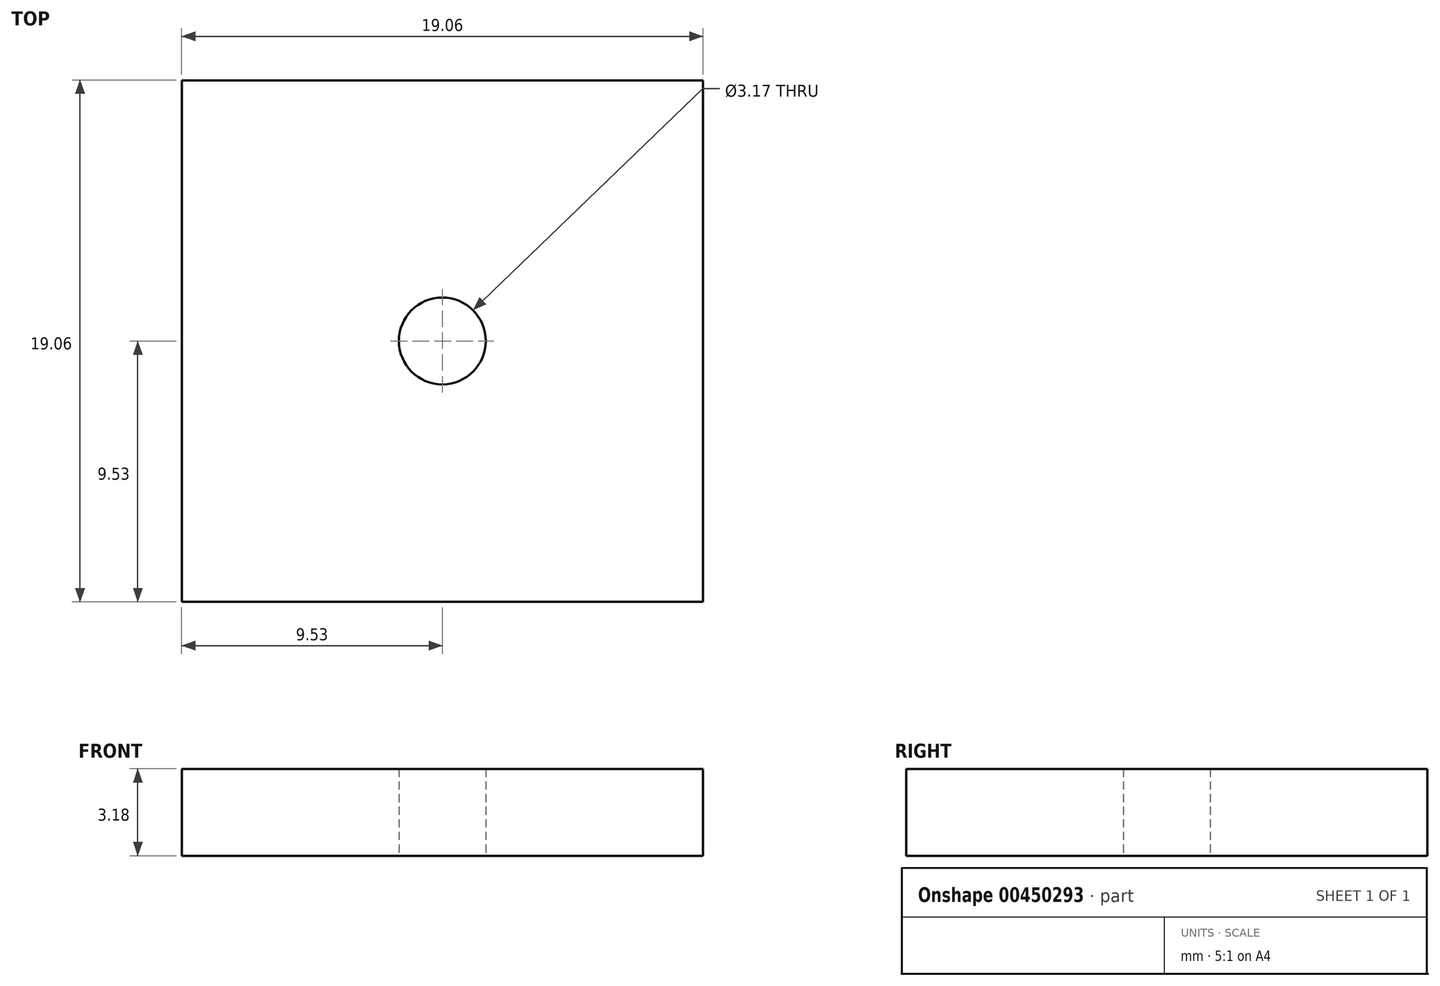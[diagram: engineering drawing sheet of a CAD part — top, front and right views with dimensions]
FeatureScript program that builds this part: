
annotation { "Feature Type Name" : "Feature", "Feature Type Description" : "" }
export const myFeature = defineFeature(function(context is Context, id is Id, definition is map)
    precondition{}
    {
        {
            var Q0;
            Q0=qCreatedBy(makeId("Top.planeOp"),FACE);
            var sketch = newSketch(context, id + "F0", { "sketchPlane" : qUnion([Q0])});
            skLineSegment(sketch, "E0.bottom", {"start": v(-9.52, -9.52) * mm, "end": v(9.53, -9.52) * mm});
            skLineSegment(sketch, "E0.top", {"start": v(-9.53, 9.52) * mm, "end": v(9.52, 9.52) * mm});
            skLineSegment(sketch, "E0.left", {"start": v(-9.52, -9.52) * mm, "end": v(-9.53, 9.52) * mm});
            skLineSegment(sketch, "E0.right", {"start": v(9.53, -9.52) * mm, "end": v(9.52, 9.52) * mm});
            skPoint(sketch, "E0.middle", {"position": v(0, 0) * mm});
            skCircle(sketch, "E1", {"center": v(0, 0) * mm, "radius": 1.59 * mm});
            skSolve(sketch);
        }
        {
            var Q0;
            Q0=makeQuery(id+"F0.imprint","IMPRINT",FACE,{"disambiguationData":[TD([[makeQuery(id+"F0.imprint","IMPRINT",EDGE,{"derivedFrom":sQuery(id+"F0.wireOp",EDGE,"E0.bottom")}),1.0]])]});
            extrude(context, id + "F1", {"entities" : qUnion([Q0]), "depth" : 3.17 * mm});
        }
    });
